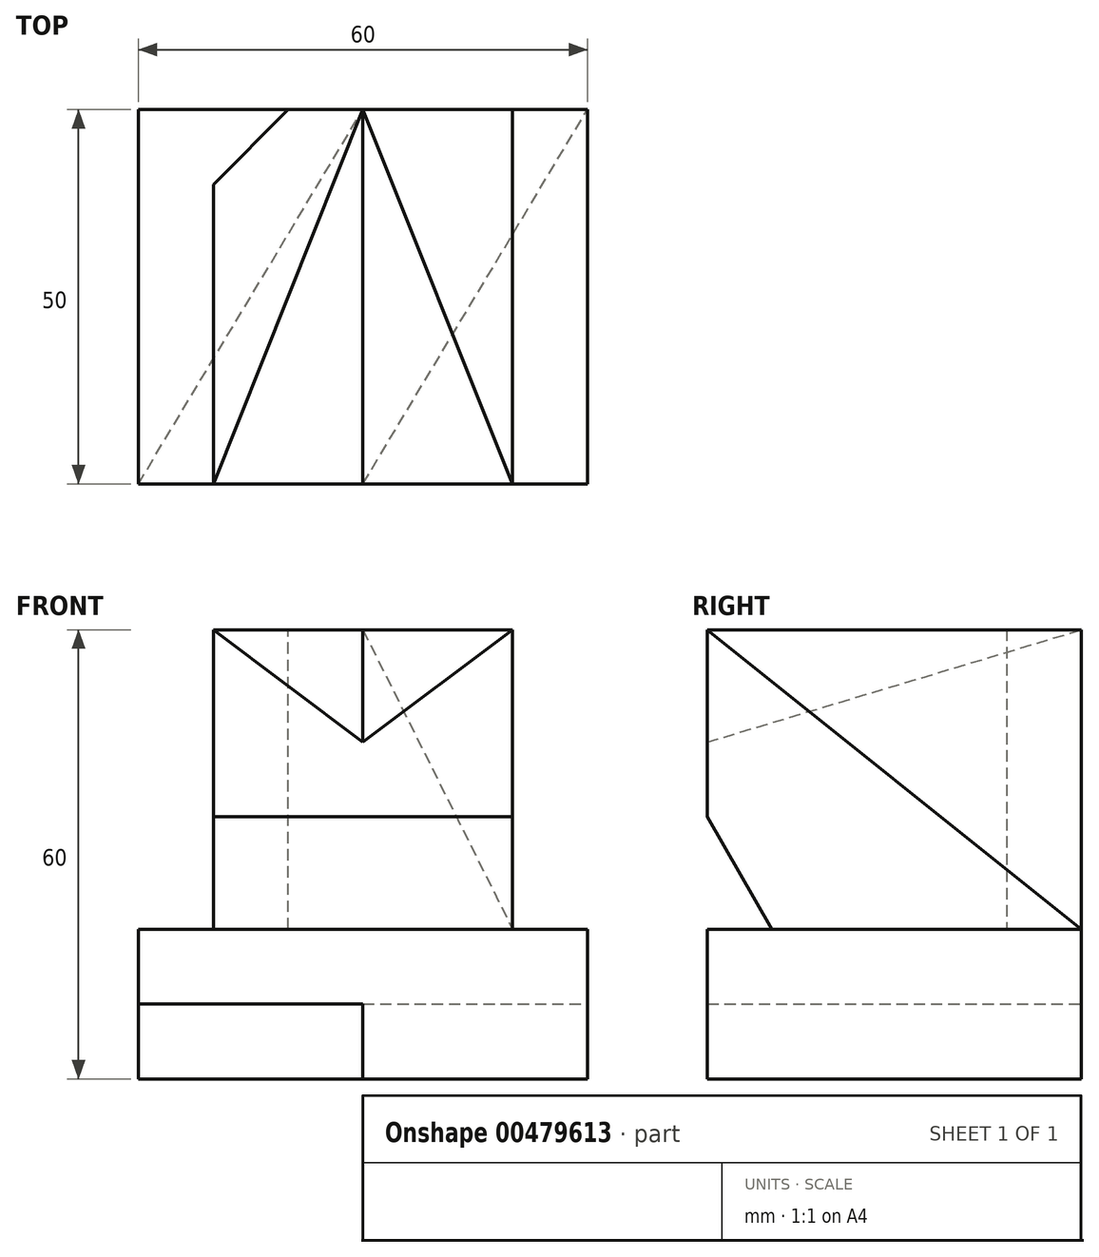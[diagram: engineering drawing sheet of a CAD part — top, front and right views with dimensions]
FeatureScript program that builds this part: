
annotation { "Feature Type Name" : "Feature", "Feature Type Description" : "" }
export const myFeature = defineFeature(function(context is Context, id is Id, definition is map)
    precondition{}
    {
        {
            var Q0;
            Q0=qCreatedBy(makeId("Front.planeOp"),FACE);
            var sketch = newSketch(context, id + "F0", { "sketchPlane" : qUnion([Q0])});
            skLineSegment(sketch, "E0.bottom", {"start": v(0, 0) * mm, "end": v(60, 0) * mm});
            skLineSegment(sketch, "E0.top", {"start": v(0, 20) * mm, "end": v(60, 20) * mm});
            skLineSegment(sketch, "E0.left", {"start": v(0, 0) * mm, "end": v(0, 20) * mm});
            skLineSegment(sketch, "E0.right", {"start": v(60, 0) * mm, "end": v(60, 20) * mm});
            skLineSegment(sketch, "E1", {"start": v(0, 20) * mm, "end": v(10, 20) * mm});
            skLineSegment(sketch, "E2", {"start": v(10, 20) * mm, "end": v(10, 60) * mm});
            skLineSegment(sketch, "E3", {"start": v(10, 60) * mm, "end": v(50, 60) * mm});
            skLineSegment(sketch, "E4", {"start": v(50, 60) * mm, "end": v(50, 20) * mm});
            skSolve(sketch);
        }
        {
            var Q0;
            Q0 = qSketchRegion(id + "F0", true);
            extrude(context, id + "F1", {"entities" : qUnion([Q0]), "oppositeDirection" : true, "depth" : 50 * mm, "offsetDistance" : 25 * mm});
        }
        {
            var Q0;
            Q0=makeQuery(id+"F1.opExtrude","SWEPT_FACE",FACE,{"disambiguationData":[OSD([sQuery(id+"F0.wireOp",EDGE,"E0.bottom")])]});
            var sketch = newSketch(context, id + "F2", { "sketchPlane" : qUnion([Q0])});
            skLineSegment(sketch, "E5", {"start": v(0, 0) * mm, "end": v(30, -50) * mm});
            skLineSegment(sketch, "E6", {"start": v(30, 0) * mm, "end": v(60, -50) * mm});
            skSolve(sketch);
        }
        {
            var Q0;
            Q0 = qSketchRegion(id + "F2", true);
            var Q1;
            {var subQ0=sQuery(id+"F2.wireOp",EDGE,"E5");Q1=makeQuery(id+"F2.imprint","IMPRINT",FACE,{"disambiguationData":[TD([[makeQuery(id+"F2.imprint","IMPRINT",EDGE,{"derivedFrom":subQ0}),1.0]])]});}
            extrude(context, id + "F3", {"entities" : qUnion([Q0, Q1]), "operationType" : NewBodyOperationType.REMOVE, "oppositeDirection" : true, "depth" : 10 * mm, "offsetDistance" : 25 * mm});
        }
        {
            var Q0;
            Q0=makeQuery(id+"F1.opExtrude","SWEPT_FACE",FACE,{"disambiguationData":[OSD([sQuery(id+"F0.wireOp",EDGE,"E4")])]});
            var sketch = newSketch(context, id + "F4", { "sketchPlane" : qUnion([Q0])});
            skLineSegment(sketch, "E7", {"start": v(0, 20) * mm, "end": v(0, 35) * mm});
            skLineSegment(sketch, "E8", {"start": v(0, 35) * mm, "end": v(8.66, 20) * mm});
            skSolve(sketch);
        }
        {
            var Q0;
            Q0 = qSketchRegion(id + "F4", true);
            var Q1;
            {var subQ0=sQuery(id+"F4.wireOp",EDGE,"E7");Q1=makeQuery(id+"F4.imprint","IMPRINT",FACE,{"disambiguationData":[TD([[makeQuery(id+"F4.imprint","IMPRINT",EDGE,{"derivedFrom":subQ0}),1.0]])]});}
            extrude(context, id + "F5", {"entities" : qUnion([Q0, Q1]), "operationType" : NewBodyOperationType.REMOVE, "endBound" : BoundingType.UP_TO_NEXT, "oppositeDirection" : true, "depth" : 25 * mm, "offsetDistance" : 25 * mm});
        }
        {
            var Q0;
            Q0=makeQuery(id+"F1.opExtrude","CAP_EDGE",EDGE,{"disambiguationData":[OSD([sQuery(id+"F0.wireOp",EDGE,"E2")])],"isStart":false});
            chamfer(context, id + "F6", {"entities" : qUnion([Q0]), "width" : 10 * mm, "tangentPropagation" : true});
        }
        {
            var Q0;
            {var subQ0=sQuery(id+"F0.wireOp",EDGE,"E2");var subQ1=sQuery(id+"F0.wireOp",EDGE,"E3");var subQ2=sQuery(id+"F0.wireOp",EDGE,"E4");Q0=makeQuery(id+"F5.boolean.opBoolean","SPLIT",FACE,{"disambiguationData":[TD([makeQuery(id+"F1.opExtrude","SWEPT_FACE",FACE,{"disambiguationData":[OSD([subQ0])]})])],"derivedFrom":makeQuery(id+"F1.opExtrude","CAP_FACE",FACE,{"disambiguationData":[OSD([sQuery(id+"F0.wireOp",EDGE,"E0.bottom"),sQuery(id+"F0.wireOp",EDGE,"E0.top"),sQuery(id+"F0.wireOp",EDGE,"E0.left"),sQuery(id+"F0.wireOp",EDGE,"E0.right"),sQuery(id+"F0.wireOp",EDGE,"E1"),subQ0,subQ1,subQ2])],"isStart":true})});}
            var sketch = newSketch(context, id + "F7", { "sketchPlane" : qUnion([Q0])});
            skLineSegment(sketch, "E9", {"start": v(10, 60) * mm, "end": v(30, 45) * mm});
            skLineSegment(sketch, "E10", {"start": v(30, 45) * mm, "end": v(50, 60) * mm});
            skSolve(sketch);
        }
        {
            var Q0;
            Q0=makeQuery(id+"F1.opExtrude","SWEPT_FACE",FACE,{"disambiguationData":[OSD([sQuery(id+"F0.wireOp",EDGE,"E4")])]});
            var sketch = newSketch(context, id + "F8", { "sketchPlane" : qUnion([Q0])});
            skLineSegment(sketch, "E11", {"start": v(0, 45) * mm, "end": v(50, 60) * mm});
            skSolve(sketch);
        }
        {
            var Q0;
            Q0=makeQuery(id+"F7.imprint","IMPRINT",FACE,{"disambiguationData":[TD([[makeQuery(id+"F7.imprint","IMPRINT",EDGE,{"derivedFrom":sQuery(id+"F7.wireOp",EDGE,"E9")}),1.0]])]});
            var Q1;
            Q1=sQuery(id+"F8.wireOp",EDGE,"E11");
            sweep(context, id + "F9", {"operationType" : NewBodyOperationType.REMOVE, "profiles" : qUnion([Q0]), "path" : qUnion([Q1])});
        }
        {
            var Q0;
            Q0=makeQuery(id+"F1.opExtrude","CAP_FACE",FACE,{"disambiguationData":[OSD([sQuery(id+"F0.wireOp",EDGE,"E0.bottom"),sQuery(id+"F0.wireOp",EDGE,"E0.top"),sQuery(id+"F0.wireOp",EDGE,"E0.left"),sQuery(id+"F0.wireOp",EDGE,"E0.right"),sQuery(id+"F0.wireOp",EDGE,"E1"),sQuery(id+"F0.wireOp",EDGE,"E2"),sQuery(id+"F0.wireOp",EDGE,"E3"),sQuery(id+"F0.wireOp",EDGE,"E4")])],"isStart":false});
            var sketch = newSketch(context, id + "F10", { "sketchPlane" : qUnion([Q0])});
            skLineSegment(sketch, "E12", {"start": v(-30, 60) * mm, "end": v(-50, 20) * mm});
            skSolve(sketch);
        }
        {
            var Q0;
            Q0=makeQuery(id+"F1.opExtrude","SWEPT_FACE",FACE,{"disambiguationData":[OSD([sQuery(id+"F0.wireOp",EDGE,"E4")])]});
            var sketch = newSketch(context, id + "F11", { "sketchPlane" : qUnion([Q0])});
            skLineSegment(sketch, "E13", {"start": v(0, 60) * mm, "end": v(50, 20) * mm});
            skSolve(sketch);
        }
        {
            var Q0;
            Q0=makeQuery(id+"F10.imprint","IMPRINT",FACE,{"disambiguationData":[TD([[makeQuery(id+"F10.imprint","IMPRINT",EDGE,{"derivedFrom":sQuery(id+"F10.wireOp",EDGE,"E12")}),-1.0]])]});
            var Q1;
            Q1=sQuery(id+"F11.wireOp",EDGE,"E13");
            sweep(context, id + "F12", {"operationType" : NewBodyOperationType.REMOVE, "profiles" : qUnion([Q0]), "path" : qUnion([Q1])});
        }
    });
